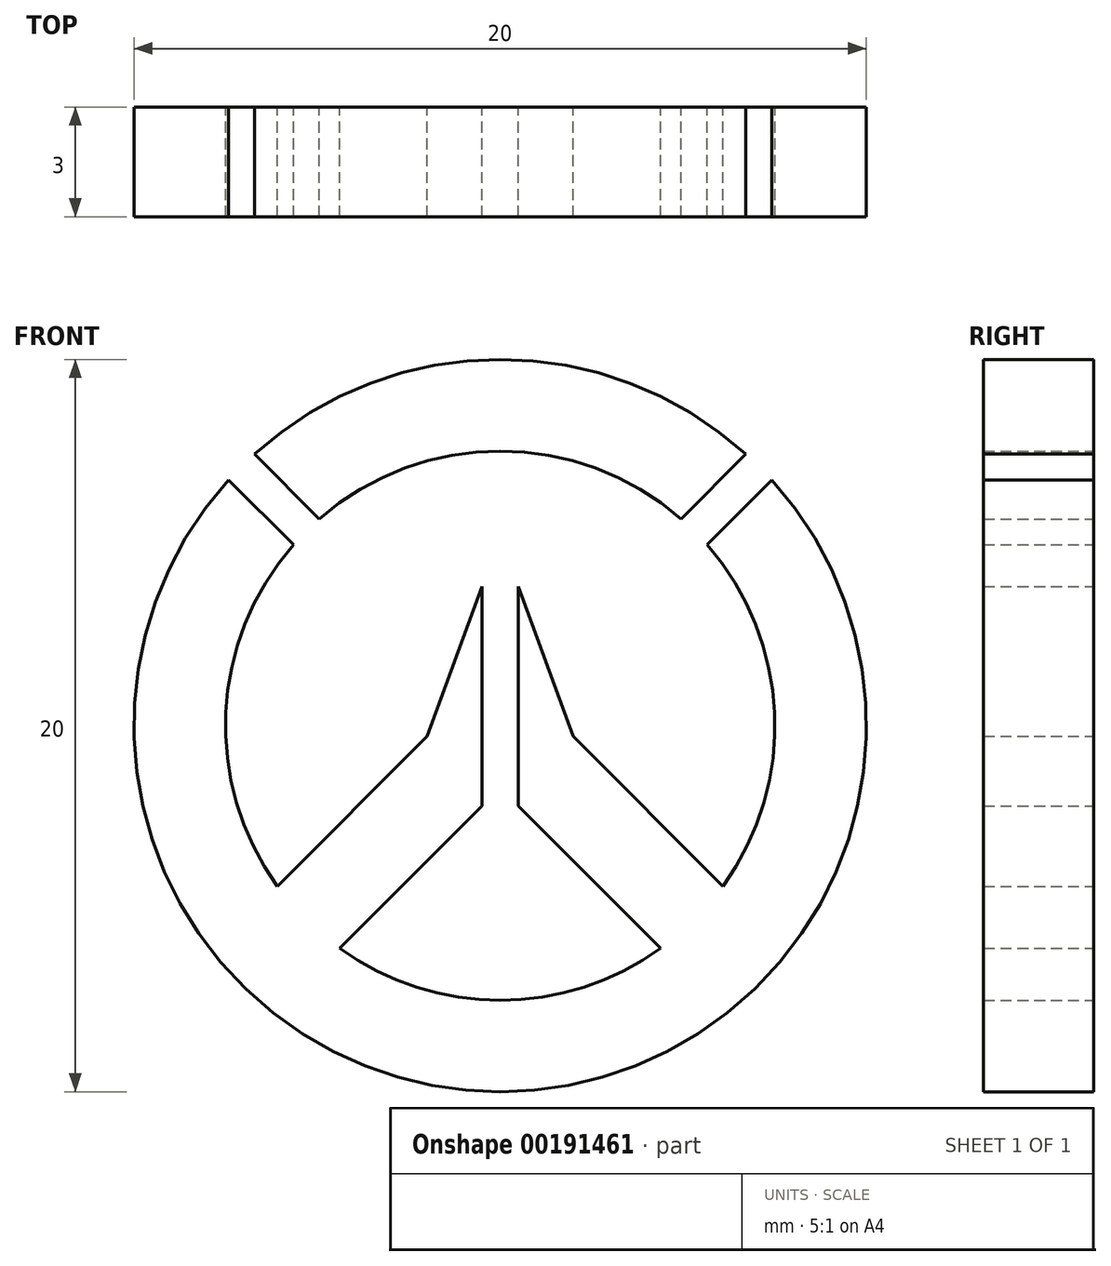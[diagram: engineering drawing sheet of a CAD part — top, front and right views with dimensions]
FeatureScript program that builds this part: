
annotation { "Feature Type Name" : "Feature", "Feature Type Description" : "" }
export const myFeature = defineFeature(function(context is Context, id is Id, definition is map)
    precondition{}
    {
        {
            var Q0;
            Q0=qCreatedBy(makeId("Front.planeOp"),FACE);
            var sketch = newSketch(context, id + "F0", { "sketchPlane" : qUnion([Q0])});
            skCircle(sketch, "E0", {"center": v(0, 0) * mm, "radius": 10 * mm});
            skCircle(sketch, "E1.0", {"center": v(0, 0) * mm, "radius": 7.5 * mm});
            skLineSegment(sketch, "E2", {"start": v(0, 0) * mm, "end": v(-7.07, 7.07) * mm, "construction": true});
            skLineSegment(sketch, "E3", {"start": v(0, 0) * mm, "end": v(7.07, 7.07) * mm, "construction": true});
            skLineSegment(sketch, "E4", {"start": v(0, 0) * mm, "end": v(0, 10) * mm, "construction": true});
            skLineSegment(sketch, "E5.0", {"start": v(0, -0.7) * mm, "end": v(-7.42, 6.7) * mm});
            skLineSegment(sketch, "E5.1", {"start": v(0, -0.7) * mm, "end": v(7.42, 6.7) * mm});
            skLineSegment(sketch, "E6.0", {"start": v(0, 0.7) * mm, "end": v(-6.7, 7.42) * mm});
            skLineSegment(sketch, "E6.1", {"start": v(0, 0.7) * mm, "end": v(6.7, 7.42) * mm});
            skSolve(sketch);
        }
        {
            var Q0;
            {var subQ0=sQuery(id+"F0.wireOp",EDGE,"E5.0");var subQ1=sQuery(id+"F0.wireOp",EDGE,"E0");var subQ2=makeQuery(id+"F0.imprint","INTERSECT",VERTEX,{"derivedFrom":[subQ1,subQ0]});Q0=makeQuery(id+"F0.imprint","IMPRINT",FACE,{"disambiguationData":[TD([[makeQuery(id+"F0.imprint","IMPRINT",EDGE,{"disambiguationData":[TD([[subQ2,-1.0]])],"derivedFrom":subQ1}),1.0]])]});}
            extrude(context, id + "F1", {"entities" : qUnion([Q0]), "depth" : 3 * mm});
        }
        {
            var Q0;
            {var subQ0=sQuery(id+"F0.wireOp",EDGE,"E6.0");var subQ1=sQuery(id+"F0.wireOp",EDGE,"E0");var subQ2=makeQuery(id+"F0.imprint","INTERSECT",VERTEX,{"derivedFrom":[subQ1,subQ0]});Q0=makeQuery(id+"F0.imprint","IMPRINT",FACE,{"disambiguationData":[TD([[makeQuery(id+"F0.imprint","IMPRINT",EDGE,{"disambiguationData":[TD([[subQ2,1.0]])],"derivedFrom":subQ1}),1.0]])]});}
            var Q1;
            Q1=makeQuery(id+"F1.opExtrude","CAP_FACE",FACE,{"disambiguationData":[OSD([sQuery(id+"F0.wireOp",EDGE,"E0"),sQuery(id+"F0.wireOp",EDGE,"E1.0"),sQuery(id+"F0.wireOp",EDGE,"E5.0"),sQuery(id+"F0.wireOp",EDGE,"E5.1")])],"isStart":false});
            extrude(context, id + "F2", {"entities" : qUnion([Q0]), "endBound" : BoundingType.UP_TO_SURFACE, "endBoundEntityFace" : qUnion([Q1]), "depth" : 25 * mm});
        }
        {
            var Q0;
            Q0=qCreatedBy(makeId("Front.planeOp"),FACE);
            var sketch = newSketch(context, id + "F3", { "sketchPlane" : qUnion([Q0])});
            skArc(sketch, "E7.0", {"start": v(-5.65, 4.94) * mm, "mid": v(0, -7.5) * mm, "end": v(5.65, 4.94) * mm});
            skLineSegment(sketch, "E8", {"start": v(0, 0) * mm, "end": v(-5.3, -5.3) * mm});
            skLineSegment(sketch, "E9", {"start": v(0, 0) * mm, "end": v(5.3, -5.3) * mm});
            skLineSegment(sketch, "E10", {"start": v(0, 0) * mm, "end": v(0, -7.5) * mm, "construction": true});
            skLineSegment(sketch, "E11.0", {"start": v(0, 1.7) * mm, "end": v(-6.13, -4.43) * mm});
            skLineSegment(sketch, "E11.1", {"start": v(0, 1.7) * mm, "end": v(6.15, -4.45) * mm});
            skLineSegment(sketch, "E12.0", {"start": v(0, -1.7) * mm, "end": v(-4.45, -6.15) * mm});
            skLineSegment(sketch, "E12.1", {"start": v(0, -1.7) * mm, "end": v(4.45, -6.15) * mm});
            skLineSegment(sketch, "E13", {"start": v(0, -1.7) * mm, "end": v(0, 3.8) * mm, "construction": true});
            skLineSegment(sketch, "E14.0", {"start": v(0.5, -2.2) * mm, "end": v(0.5, 3.8) * mm});
            skLineSegment(sketch, "E15.0", {"start": v(-0.5, -2.2) * mm, "end": v(-0.5, 3.8) * mm});
            skLineSegment(sketch, "E16", {"start": v(-0.5, 3.8) * mm, "end": v(-2, -0.3) * mm});
            skLineSegment(sketch, "E17", {"start": v(0.5, 3.8) * mm, "end": v(2, -0.3) * mm});
            skSolve(sketch);
        }
        {
            var Q0;
            {var subQ4=sQuery(id+"F3.wireOp",EDGE,"E8");var subQ5=sQuery(id+"F3.wireOp",EDGE,"E7.0");var subQ6=makeQuery(id+"F3.imprint","INTERSECT",VERTEX,{"derivedFrom":[subQ5,subQ4]});Q0=makeQuery(id+"F3.imprint","IMPRINT",FACE,{"disambiguationData":[TD([[makeQuery(id+"F3.imprint","IMPRINT",EDGE,{"disambiguationData":[TD([[subQ6,1.0]])],"derivedFrom":subQ5}),1.0]])]});}
            var Q1;
            {var subQ0=sQuery(id+"F3.wireOp",EDGE,"E8");var subQ1=sQuery(id+"F3.wireOp",EDGE,"E7.0");var subQ2=makeQuery(id+"F3.imprint","INTERSECT",VERTEX,{"derivedFrom":[subQ1,subQ0]});Q1=makeQuery(id+"F3.imprint","IMPRINT",FACE,{"disambiguationData":[TD([[makeQuery(id+"F3.imprint","IMPRINT",EDGE,{"disambiguationData":[TD([[subQ2,-1.0]])],"derivedFrom":subQ1}),1.0]])]});}
            var Q2;
            {var subQ0=sQuery(id+"F3.wireOp",EDGE,"E16");Q2=makeQuery(id+"F3.imprint","IMPRINT",FACE,{"disambiguationData":[TD([[makeQuery(id+"F3.imprint","IMPRINT",EDGE,{"derivedFrom":subQ0}),1.0]])]});}
            var Q3;
            {var subQ2=sQuery(id+"F3.wireOp",EDGE,"E7.0");var subQ4=sQuery(id+"F3.wireOp",EDGE,"E9");var subQ5=makeQuery(id+"F3.imprint","INTERSECT",VERTEX,{"derivedFrom":[subQ2,subQ4]});Q3=makeQuery(id+"F3.imprint","IMPRINT",FACE,{"disambiguationData":[TD([[makeQuery(id+"F3.imprint","IMPRINT",EDGE,{"disambiguationData":[TD([[subQ5,-1.0]])],"derivedFrom":subQ2}),1.0]])]});}
            var Q4;
            {var subQ0=sQuery(id+"F3.wireOp",EDGE,"E9");var subQ1=sQuery(id+"F3.wireOp",EDGE,"E7.0");var subQ2=makeQuery(id+"F3.imprint","INTERSECT",VERTEX,{"derivedFrom":[subQ1,subQ0]});Q4=makeQuery(id+"F3.imprint","IMPRINT",FACE,{"disambiguationData":[TD([[makeQuery(id+"F3.imprint","IMPRINT",EDGE,{"disambiguationData":[TD([[subQ2,1.0]])],"derivedFrom":subQ1}),1.0]])]});}
            var Q5;
            {var subQ0=sQuery(id+"F3.wireOp",EDGE,"E17");Q5=makeQuery(id+"F3.imprint","IMPRINT",FACE,{"disambiguationData":[TD([[makeQuery(id+"F3.imprint","IMPRINT",EDGE,{"derivedFrom":subQ0}),-1.0]])]});}
            var Q6;
            Q6=makeQuery(id+"F1.opExtrude","CAP_FACE",FACE,{"disambiguationData":[OSD([sQuery(id+"F0.wireOp",EDGE,"E0"),sQuery(id+"F0.wireOp",EDGE,"E1.0"),sQuery(id+"F0.wireOp",EDGE,"E5.0"),sQuery(id+"F0.wireOp",EDGE,"E5.1")])],"isStart":false});
            extrude(context, id + "F4", {"entities" : qUnion([Q0, Q1, Q2, Q3, Q4, Q5]), "operationType" : NewBodyOperationType.ADD, "endBound" : BoundingType.UP_TO_SURFACE, "endBoundEntityFace" : qUnion([Q6]), "depth" : 25 * mm});
        }
    });
